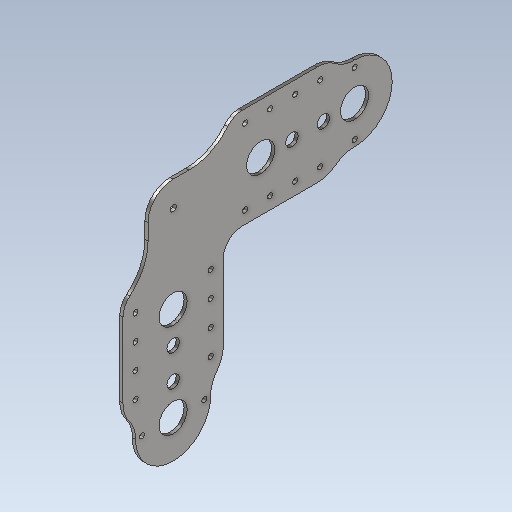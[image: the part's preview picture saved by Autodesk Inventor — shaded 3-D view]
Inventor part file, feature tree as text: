
AUTODESK INVENTOR PART (.ipt)
format: ipt  version: 2023 (Build 270158000, 158)  size: 194,048 bytes
history: native  units: in
note: dims shown in document units (in); Inventor stores cm internally (conversion verified against a paired STEP export)
features: other x3, sketch x1
ambient origin geometry x8: Origin, YZ Plane, XZ Plane, XY Plane, X Axis, Y Axis, Z Axis, Center Point
bodies: Solid1 (feature_tree)
feature tree (4):
  other  "L3Plate.ipt"
  other  "Solid1::L3Plate.ipt"
  other  "TaggingFeature1"
  sketch  "Sketch1"  dims[d0=0.3937in]
